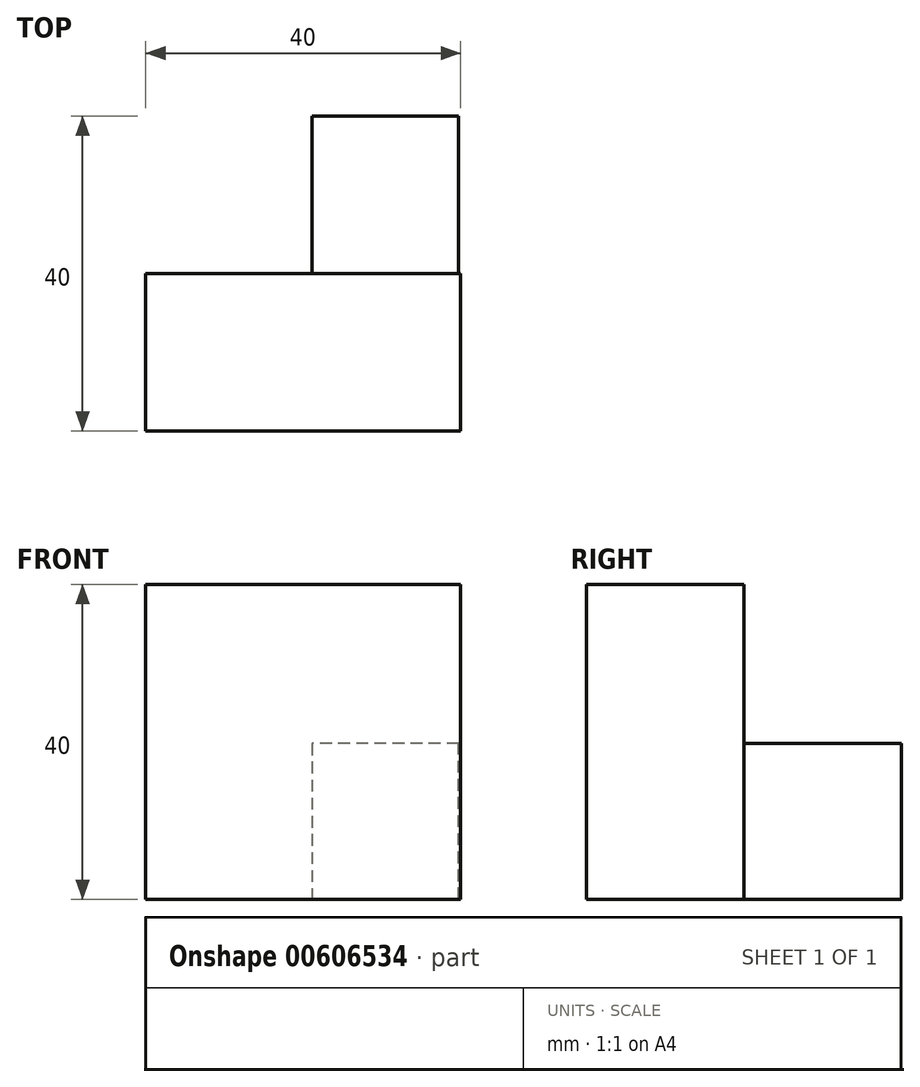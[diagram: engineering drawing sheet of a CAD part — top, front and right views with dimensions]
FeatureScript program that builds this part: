
annotation { "Feature Type Name" : "Feature", "Feature Type Description" : "" }
export const myFeature = defineFeature(function(context is Context, id is Id, definition is map)
    precondition{}
    {
        {
            var Q0;
            Q0=qCreatedBy(makeId("Front.planeOp"),FACE);
            var sketch = newSketch(context, id + "F0", { "sketchPlane" : qUnion([Q0])});
            skLineSegment(sketch, "E0", {"start": v(0, 40) * mm, "end": v(0, 0) * mm});
            skLineSegment(sketch, "E1", {"start": v(0, 0) * mm, "end": v(40, 0) * mm});
            skLineSegment(sketch, "E2", {"start": v(40, 0) * mm, "end": v(40, 40) * mm});
            skLineSegment(sketch, "E3", {"start": v(40, 40) * mm, "end": v(0, 40) * mm});
            skSolve(sketch);
        }
        {
            var Q0;
            Q0 = qSketchRegion(id + "F0", true);
            extrude(context, id + "F1", {"entities" : qUnion([Q0]), "depth" : 20 * mm, "offsetDistance" : 25 * mm});
        }
        {
            var Q0;
            Q0=qCreatedBy(makeId("Front.planeOp"),FACE);
            var sketch = newSketch(context, id + "F2", { "sketchPlane" : qUnion([Q0])});
            skLineSegment(sketch, "E4", {"start": v(21.15, 0) * mm, "end": v(39.75, 0) * mm});
            skLineSegment(sketch, "E5", {"start": v(39.75, 0) * mm, "end": v(39.75, 19.8) * mm});
            skLineSegment(sketch, "E6", {"start": v(39.75, 19.8) * mm, "end": v(21.15, 19.8) * mm});
            skLineSegment(sketch, "E7", {"start": v(21.15, 19.8) * mm, "end": v(21.15, 0) * mm});
            skSolve(sketch);
        }
        {
            var Q0;
            Q0 = qSketchRegion(id + "F2", true);
            extrude(context, id + "F3", {"entities" : qUnion([Q0]), "operationType" : NewBodyOperationType.ADD, "depth" : -20 * mm, "offsetDistance" : 25 * mm});
        }
    });
